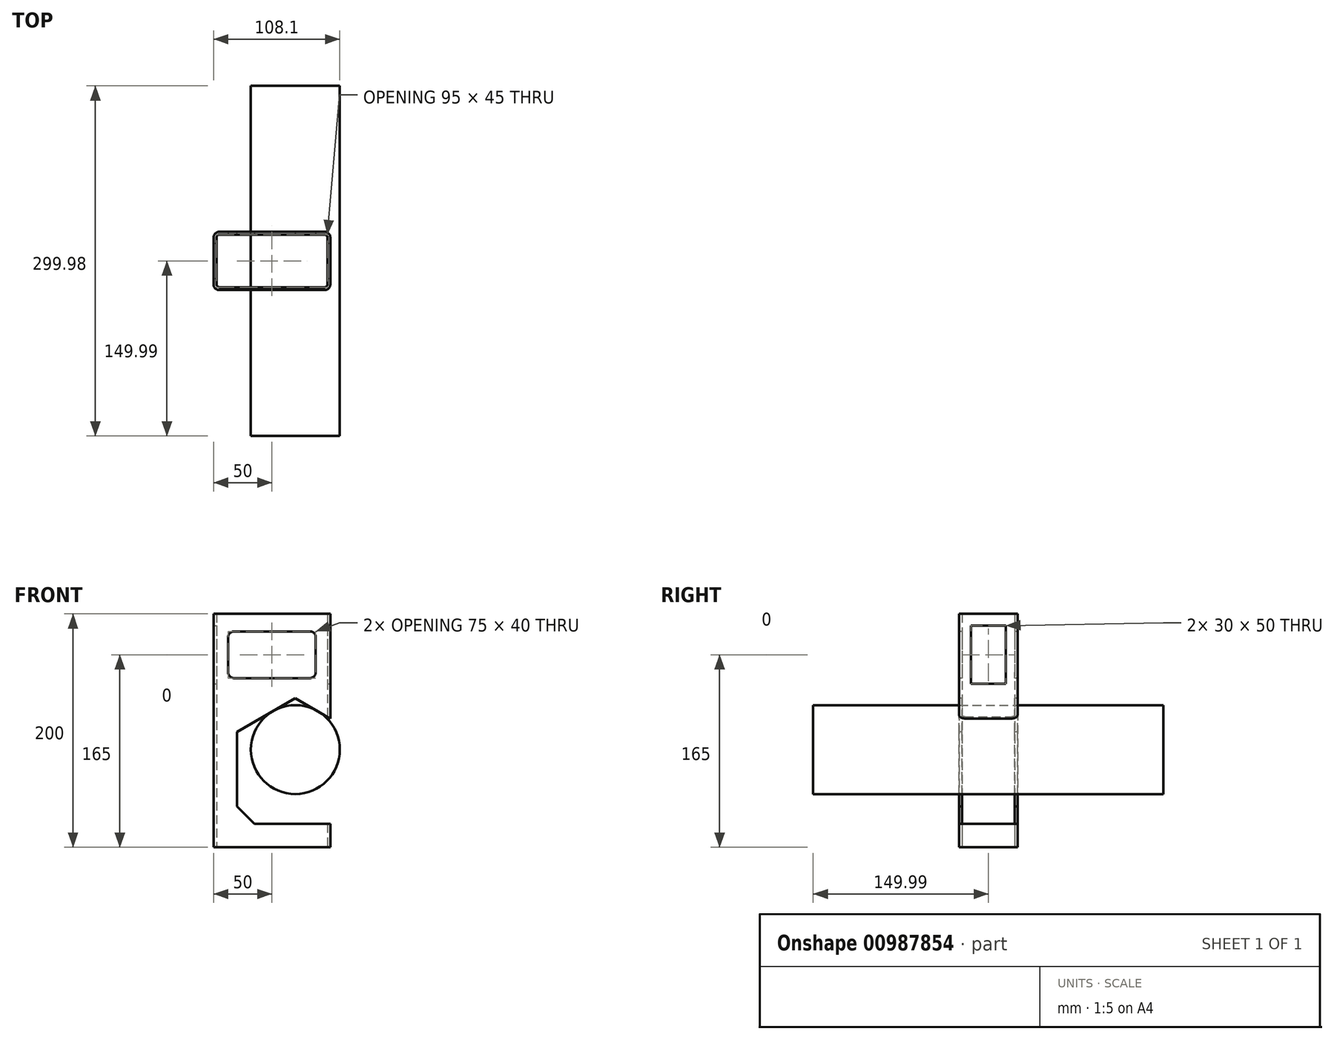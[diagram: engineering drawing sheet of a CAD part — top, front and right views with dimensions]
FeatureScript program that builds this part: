
annotation { "Feature Type Name" : "Feature", "Feature Type Description" : "" }
export const myFeature = defineFeature(function(context is Context, id is Id, definition is map)
    precondition{}
    {
        {
            var Q0;
            Q0=qCreatedBy(makeId("Top.planeOp"),FACE);
            var sketch = newSketch(context, id + "F0", { "sketchPlane" : qUnion([Q0])});
            skLineSegment(sketch, "E0.bottom", {"start": v(50, 25) * mm, "end": v(-50, 25) * mm});
            skLineSegment(sketch, "E0.top", {"start": v(50, -25) * mm, "end": v(-50, -25) * mm});
            skLineSegment(sketch, "E0.left", {"start": v(50, 25) * mm, "end": v(50, -25) * mm});
            skLineSegment(sketch, "E0.right", {"start": v(-50, 25) * mm, "end": v(-50, -25) * mm});
            skPoint(sketch, "E0.middle", {"position": v(0, 0) * mm});
            skSolve(sketch);
        }
        {
            var Q0;
            Q0=qSketchRegion(id+"F0",true);
            extrude(context, id + "F1", {"entities" : qUnion([Q0]), "endBound" : BoundingType.SYMMETRIC, "depth" : 200 * mm, "offsetDistance" : 25 * mm});
        }
        {
            var Q0;
            Q0=makeQuery(id+"F1.opExtrude","SWEPT_EDGE",EDGE,{"disambiguationData":[OSD([sQuery(id+"F0.wireOp",EDGE,"E0.top"),sQuery(id+"F0.wireOp",EDGE,"E0.right")])]});
            var Q1;
            Q1=makeQuery(id+"F1.opExtrude","SWEPT_EDGE",EDGE,{"disambiguationData":[OSD([sQuery(id+"F0.wireOp",EDGE,"E0.bottom"),sQuery(id+"F0.wireOp",EDGE,"E0.right")])]});
            var Q2;
            Q2=makeQuery(id+"F1.opExtrude","SWEPT_EDGE",EDGE,{"disambiguationData":[OSD([sQuery(id+"F0.wireOp",EDGE,"E0.top"),sQuery(id+"F0.wireOp",EDGE,"E0.left")])]});
            var Q3;
            Q3=makeQuery(id+"F1.opExtrude","SWEPT_EDGE",EDGE,{"disambiguationData":[OSD([sQuery(id+"F0.wireOp",EDGE,"E0.bottom"),sQuery(id+"F0.wireOp",EDGE,"E0.left")])]});
            fillet(context, id + "F2", {"entities" : qUnion([Q0, Q1, Q2, Q3]), "radius" : 5 * mm, "tangentPropagation" : true, "allowEdgeOverflow" : false});
        }
        {
            var Q0;
            Q0=makeQuery(id+"F1.opExtrude","CAP_FACE",FACE,{"disambiguationData":[OSD([sQuery(id+"F0.wireOp",EDGE,"E0.bottom"),sQuery(id+"F0.wireOp",EDGE,"E0.top"),sQuery(id+"F0.wireOp",EDGE,"E0.left"),sQuery(id+"F0.wireOp",EDGE,"E0.right")])],"isStart":false});
            var Q1;
            Q1=makeQuery(id+"F1.opExtrude","CAP_FACE",FACE,{"disambiguationData":[OSD([sQuery(id+"F0.wireOp",EDGE,"E0.bottom"),sQuery(id+"F0.wireOp",EDGE,"E0.top"),sQuery(id+"F0.wireOp",EDGE,"E0.left"),sQuery(id+"F0.wireOp",EDGE,"E0.right")])],"isStart":true});
            shell(context, id + "F3", {"entities" : qUnion([Q0, Q1]), "thickness" : 2.5 * mm});
        }
        {
            var Q0;
            Q0=qCreatedBy(makeId("Right.planeOp"),FACE);
            var sketch = newSketch(context, id + "F4", { "sketchPlane" : qUnion([Q0])});
            skLineSegment(sketch, "E1.bottom", {"start": v(15, 90) * mm, "end": v(-15, 90) * mm});
            skLineSegment(sketch, "E1.top", {"start": v(15, 40) * mm, "end": v(-15, 40) * mm});
            skLineSegment(sketch, "E1.left", {"start": v(15, 90) * mm, "end": v(15, 40) * mm});
            skLineSegment(sketch, "E1.right", {"start": v(-15, 90) * mm, "end": v(-15, 40) * mm});
            skPoint(sketch, "E1.middle", {"position": v(0, 65) * mm});
            skSolve(sketch);
        }
        {
            var Q0;
            Q0=qSketchRegion(id+"F4",true);
            extrude(context, id + "F5", {"entities" : qUnion([Q0]), "operationType" : NewBodyOperationType.REMOVE, "endBound" : BoundingType.SYMMETRIC, "oppositeDirection" : true, "depth" : 220 * mm, "offsetDistance" : 25 * mm});
        }
        {
            var Q0;
            Q0=qCreatedBy(makeId("Front.planeOp"),FACE);
            var sketch = newSketch(context, id + "F6", { "sketchPlane" : qUnion([Q0])});
            skCircle(sketch, "E2", {"center": v(20, -30) * mm, "radius": 50 * mm, "construction": true});
            skLineSegment(sketch, "E3", {"start": v(20, -30) * mm, "end": v(20, 72.6) * mm, "construction": true});
            skLineSegment(sketch, "E4", {"start": v(-30, -1.13) * mm, "end": v(20, 27.74) * mm});
            skLineSegment(sketch, "E5", {"start": v(20, 27.74) * mm, "end": v(90.14, -12.76) * mm});
            skLineSegment(sketch, "E6", {"start": v(90.14, -80) * mm, "end": v(-30, -80) * mm});
            skLineSegment(sketch, "E7", {"start": v(-30, -80) * mm, "end": v(-30, -1.13) * mm});
            skLineSegment(sketch, "E8", {"start": v(90.14, -12.76) * mm, "end": v(90.14, -80) * mm});
            skSolve(sketch);
        }
        {
            var Q0;
            Q0=qSketchRegion(id+"F6",true);
            extrude(context, id + "F7", {"entities" : qUnion([Q0]), "operationType" : NewBodyOperationType.REMOVE, "endBound" : BoundingType.SYMMETRIC, "oppositeDirection" : true, "depth" : 86.6 * mm, "offsetDistance" : 25 * mm});
        }
        {
            var Q0;
            {var subQ0=sQuery(id+"F0.wireOp",EDGE,"E0.top");var subQ1=sQuery(id+"F6.wireOp",EDGE,"E6");var subQ2=sQuery(id+"F6.wireOp",EDGE,"E7");Q0=makeQuery(id+"F7.boolean.opBoolean","COPY",EDGE,{"disambiguationData":[TD([makeQuery(id+"F1.opExtrude","SWEPT_FACE",FACE,{"disambiguationData":[OSD([subQ0])]})])],"derivedFrom":makeQuery(id+"F7.opExtrude","SWEPT_EDGE",EDGE,{"disambiguationData":[OSD([subQ1,subQ2])]})});}
            var Q1;
            {var subQ0=sQuery(id+"F0.wireOp",EDGE,"E0.bottom");var subQ1=sQuery(id+"F6.wireOp",EDGE,"E6");var subQ2=sQuery(id+"F6.wireOp",EDGE,"E7");Q1=makeQuery(id+"F7.boolean.opBoolean","COPY",EDGE,{"disambiguationData":[TD([makeQuery(id+"F1.opExtrude","SWEPT_FACE",FACE,{"disambiguationData":[OSD([subQ0])]})])],"derivedFrom":makeQuery(id+"F7.opExtrude","SWEPT_EDGE",EDGE,{"disambiguationData":[OSD([subQ1,subQ2])]})});}
            chamfer(context, id + "F8", {"entities" : qUnion([Q0, Q1]), "width" : 15 * mm, "tangentPropagation" : true});
        }
        {
            var Q0;
            Q0=makeQuery(id+"F1.opExtrude","SWEPT_FACE",FACE,{"disambiguationData":[OSD([sQuery(id+"F0.wireOp",EDGE,"E0.top")])]});
            var sketch = newSketch(context, id + "F9", { "sketchPlane" : qUnion([Q0])});
            skLineSegment(sketch, "E9.bottom", {"start": v(32.5, 85) * mm, "end": v(-32.5, 85) * mm});
            skLineSegment(sketch, "E9.top", {"start": v(32.5, 45) * mm, "end": v(-32.5, 45) * mm});
            skLineSegment(sketch, "E9.left", {"start": v(37.5, 80) * mm, "end": v(37.5, 50) * mm});
            skLineSegment(sketch, "E9.right", {"start": v(-37.5, 80) * mm, "end": v(-37.5, 50) * mm});
            skPoint(sketch, "E9.middle", {"position": v(0, 65) * mm});
            skPoint(sketch, "E10.visualSharp", {"position": v(37.5, 45) * mm});
            skArc(sketch, "E10.filletArc", {"start": v(32.5, 45) * mm, "mid": v(36.04, 46.46) * mm, "end": v(37.5, 50) * mm});
            skPoint(sketch, "E11.visualSharp", {"position": v(-37.5, 45) * mm});
            skArc(sketch, "E11.filletArc", {"start": v(-37.5, 50) * mm, "mid": v(-36.04, 46.46) * mm, "end": v(-32.5, 45) * mm});
            skPoint(sketch, "E12.visualSharp", {"position": v(-37.5, 85) * mm});
            skArc(sketch, "E12.filletArc", {"start": v(-32.5, 85) * mm, "mid": v(-36.04, 83.54) * mm, "end": v(-37.5, 80) * mm});
            skPoint(sketch, "E13.visualSharp", {"position": v(37.5, 85) * mm});
            skArc(sketch, "E13.filletArc", {"start": v(37.5, 80) * mm, "mid": v(36.04, 83.54) * mm, "end": v(32.5, 85) * mm});
            skSolve(sketch);
        }
        {
            var Q0;
            Q0=qSketchRegion(id+"F9",true);
            extrude(context, id + "F10", {"entities" : qUnion([Q0]), "operationType" : NewBodyOperationType.REMOVE, "oppositeDirection" : true, "depth" : 102.46 * mm, "offsetDistance" : 25 * mm});
        }
        {
            var Q0;
            Q0=makeQuery(id+"F6.imprint","IMPRINT",FACE,{"disambiguationData":[TD([[makeQuery(id+"F6.imprint","IMPRINT",EDGE,{"derivedFrom":sQuery(id+"F6.wireOp",EDGE,"E4")}),-1.0]])]});
            var sketch = newSketch(context, id + "F11", { "sketchPlane" : qUnion([Q0])});
            skCircle(sketch, "E14", {"center": v(20, -16.26) * mm, "radius": 38.1 * mm});
            skSolve(sketch);
        }
        {
            var Q0;
            Q0=qSketchRegion(id+"F11",true);
            extrude(context, id + "F12", {"entities" : qUnion([Q0]), "endBound" : BoundingType.SYMMETRIC, "depth" : 300 * mm, "offsetDistance" : 25 * mm});
        }
        {
            var Q0;
            Q0=makeQuery(id+"F12.opExtrude","CAP_FACE",FACE,{"disambiguationData":[OSD([sQuery(id+"F11.wireOp",EDGE,"E14")])],"isStart":false});
            extrude(context, id + "F13", {"entities" : qUnion([Q0]), "operationType" : NewBodyOperationType.ADD, "oppositeDirection" : true, "depth" : 40 * mm, "offsetDistance" : 25 * mm});
        }
    });
